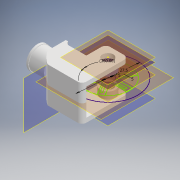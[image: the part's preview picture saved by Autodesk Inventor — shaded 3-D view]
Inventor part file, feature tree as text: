
AUTODESK INVENTOR PART (.ipt)
format: ipt  version: 2020 (Build 240168000, 168)  size: 436,736 bytes
history: native  units: mm
features: sketch x17, extrude x15, plane x8, projected_geometry x6, fillet x4, mirror x2, chamfer x1
ambient origin geometry x8: Origin, YZ Plane, XZ Plane, XY Plane, X Axis, Y Axis, Z Axis, Center Point
bodies: Solid1 (feature_tree)
feature tree (53):
  plane  "Work Plane2"
  sketch  "Sketch5"  dims[d8=0.5mm d9=0.5mm d18=6.0mm d33=7.5mm]
  plane  "Work Plane3"
  extrude  "Extrusion4"  Depth=7.5mm
  plane  "Work Plane5"
  extrude  "Extrusion5"  Depth=11.0mm
  plane  "Work Plane1"
  plane  "Work Plane4"
  extrude  "Extrusion6"  Depth=2.0mm
  plane  "Work Plane6"
  extrude  "Extrusion7"  Depth=2.0mm
  extrude  "Extrusion8"  Depth=9.0mm
  plane  "Work Plane7"
  sketch  "Sketch13"  dims[d45=13.0mm d46=2.5mm]
  extrude  "Extrusion9"  Depth=2.5mm
  sketch  "Sketch14"  dims[d47=5.0mm d48=2.0mm d49=0.0mm]
  extrude  "Extrusion10"  Depth=2.0mm TaperAngle=0.0deg
  extrude  "Extrusion11"  Depth=7.0mm
  extrude  "Extrusion12"  Depth=1.0mm
  extrude  "Extrusion13"  Depth=1.0mm TaperAngle=0.0deg
  fillet  "Fillet14"  Radius=3.5mm
  mirror  "Mirror4"
  extrude  "Extrusion14"  Depth=10.0mm TaperAngle=0.0deg
  mirror  "Mirror5"
  extrude  "Extrusion15"  Depth=2.0mm
  fillet  "Fillet15"  Radius=2.0mm
  extrude  "Extrusion16"  Depth=1.0mm TaperAngle=0.0deg
  extrude  "Extrusion17"  Depth=2.0mm
  sketch  "Sketch24"  dims[d89=1.5mm d90=0.0mm d91=2.0mm d92=10.5mm d93=1.0mm d94=0.0mm]
  chamfer  "Chamfer1"  Distance=3.25mm
  extrude  "Extrusion18"  Depth=2.0mm
  fillet  "Fillet16"  Radius=10.5mm
  fillet  "Fillet17"  Radius=1.0mm
  sketch  "Sketch6"  dims[d34=7.5mm d35=11.0mm]
  sketch  "Sketch7"  dims[d36=7.5mm d37=2.0mm]
  sketch  "Sketch10"  dims[d38=2.0mm d39=0.0mm d41=2.0mm]
  projected_geometry  "Projected Loop1"
  sketch  "Sketch12"  dims[d42=6.26mm d43=0.0mm d44=9.0mm]
  projected_geometry  "Projected Loop2"
  sketch  "Sketch15"  dims[d51=6.0mm d52=7.0mm]
  sketch  "Sketch17"  dims[d53=1.0mm d55=1.0mm]
  projected_geometry  "Projected Loop3"
  sketch  "Sketch18"  dims[d56=6.25mm d57=0.0mm d59=1.0mm d60=0.0mm d61=3.5mm]
  projected_geometry  "Projected Loop4"
  sketch  "Sketch19"  dims[d62=10.0mm d68=7.0mm d69=0.0mm]
  projected_geometry  "Projected Loop5"
  plane  "Work Plane8"
  sketch  "Sketch20"  dims[d75=2.0mm d76=0.0mm d77=6.0mm d78=2.0mm d79=0.0mm]
  sketch  "Sketch21"  dims[d80=1.0mm d81=0.0mm d82=1.0mm d83=0.0mm]
  sketch  "Sketch22"  dims[d84=2.0mm d85=5.0mm]
  sketch  "Sketch23"  dims[d86=7.0mm d87=3.25mm d88=0.0mm]
  sketch  "Sketch25"  dims[d95=6.0mm d96=0.0mm d97=0.8mm d98=2.0mm d99=45.0deg d100=13.0mm d101=1.0mm d102=0.0mm d103=2.0mm d104=2.0mm d15=0.5mm d16=0.872665mm d17=0.5mm d50=0.5mm]
  projected_geometry  "Projected Loop6"
